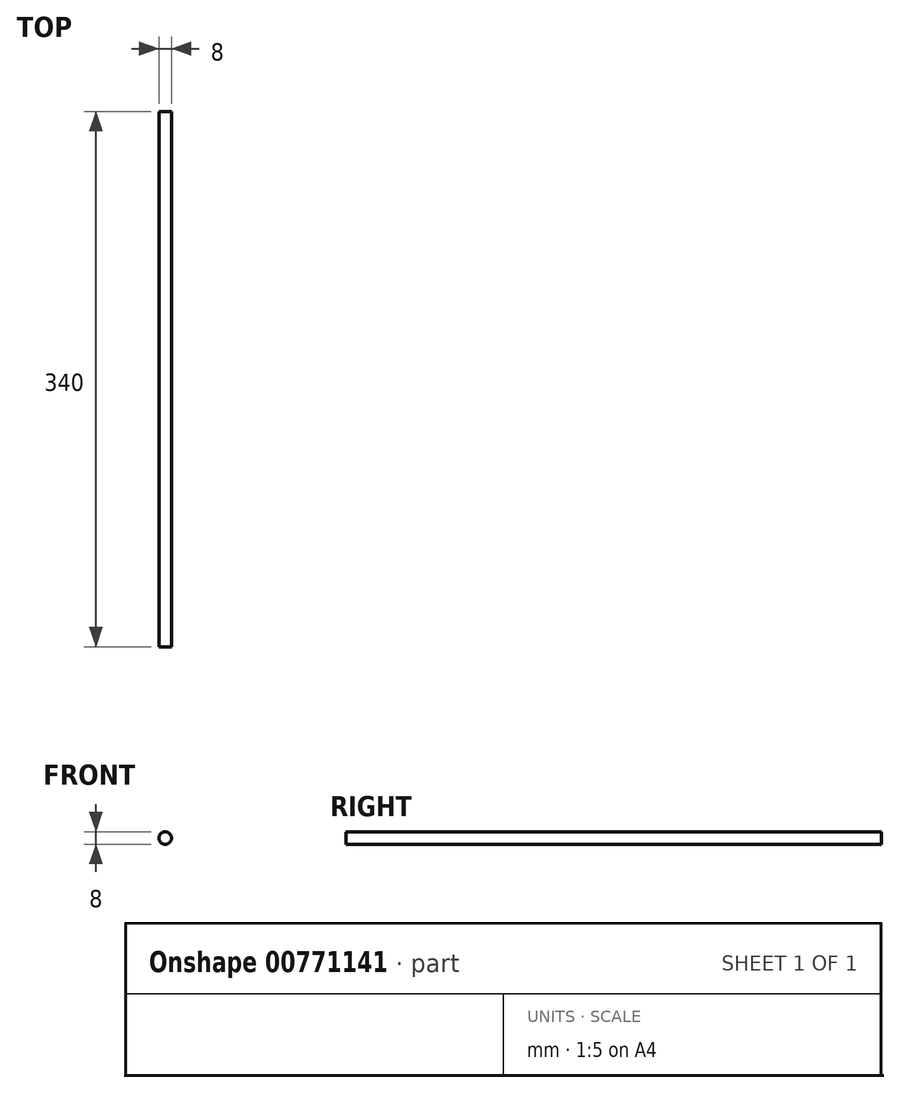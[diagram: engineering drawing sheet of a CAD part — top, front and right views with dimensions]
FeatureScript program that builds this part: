
annotation { "Feature Type Name" : "Feature", "Feature Type Description" : "" }
export const myFeature = defineFeature(function(context is Context, id is Id, definition is map)
    precondition{}
    {
        {
            var Q0;
            Q0=qCreatedBy(makeId("Front.planeOp"),FACE);
            var sketch = newSketch(context, id + "F0", { "sketchPlane" : qUnion([Q0])});
            skCircle(sketch, "E0", {"center": v(0, 0) * mm, "radius": 4 * mm});
            skSolve(sketch);
        }
        {
            var Q0;
            Q0 = qSketchRegion(id + "F0", true);
            extrude(context, id + "F1", {"entities" : qUnion([Q0]), "depth" : 340 * mm, "offsetDistance" : 25 * mm});
        }
    });
